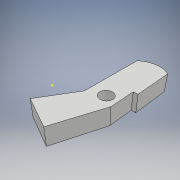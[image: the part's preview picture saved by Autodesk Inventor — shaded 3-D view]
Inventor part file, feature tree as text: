
AUTODESK INVENTOR PART (.ipt)
format: ipt  version: 2018 (Build 220112000, 112)  size: 112,128 bytes
history: native  units: mm
features: extrude x1
ambient origin geometry x8: Origin, YZ Plane, XZ Plane, XY Plane, X Axis, Y Axis, Z Axis, Center Point
bodies: Body1 (feature_tree)
feature tree (1):
  extrude  "Vysunutí3"  Depth=3.0mm
